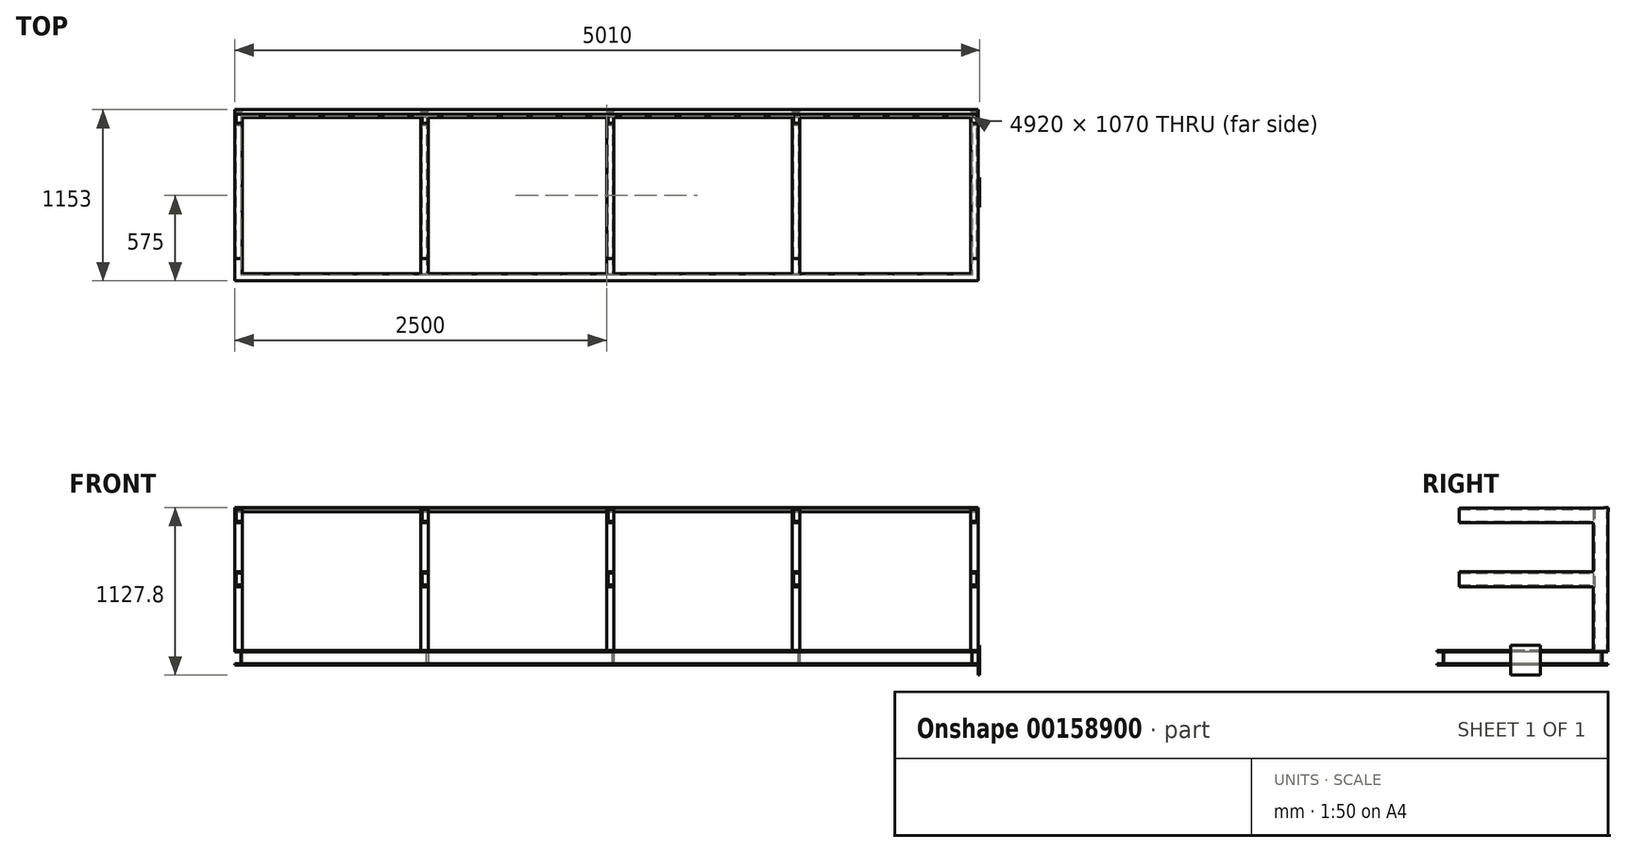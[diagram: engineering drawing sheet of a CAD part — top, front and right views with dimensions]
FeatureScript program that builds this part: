
annotation { "Feature Type Name" : "Feature", "Feature Type Description" : "" }
export const myFeature = defineFeature(function(context is Context, id is Id, definition is map)
    precondition{}
    {
        {
            var Q0;
            Q0=qCreatedBy(makeId("Top.planeOp"),FACE);
            var sketch = newSketch(context, id + "F0", { "sketchPlane" : qUnion([Q0])});
            skLineSegment(sketch, "E0.rect.bottom", {"start": v(2500, 550) * mm, "end": v(-2500, 550) * mm});
            skLineSegment(sketch, "E0.rect.top", {"start": v(2500, -600) * mm, "end": v(-2500, -600) * mm});
            skLineSegment(sketch, "E0.rect.left", {"start": v(2500, 550) * mm, "end": v(2500, -600) * mm});
            skLineSegment(sketch, "E0.rect.right", {"start": v(-2500, 550) * mm, "end": v(-2500, -600) * mm});
            skPoint(sketch, "E0.rect.middle", {"position": v(0, 0) * mm});
            skLineSegment(sketch, "E1.rect.left", {"start": v(2450, 500) * mm, "end": v(2450, -550) * mm});
            skLineSegment(sketch, "E1.rect.right", {"start": v(-2450, 500) * mm, "end": v(-2450, -550) * mm});
            skLineSegment(sketch, "E2.trimOffspring", {"start": v(2450, 500) * mm, "end": v(-2450, 500) * mm});
            skLineSegment(sketch, "E3.trimOffspring", {"start": v(2450, -550) * mm, "end": v(-2450, -550) * mm});
            skSolve(sketch);
        }
        {
            var Q0;
            Q0=makeQuery(id+"F0.imprint","IMPRINT",FACE,{"disambiguationData":[TD([[makeQuery(id+"F0.imprint","IMPRINT",EDGE,{"derivedFrom":sQuery(id+"F0.wireOp",EDGE,"E0.rect.bottom")}),1.0]])]});
            var Q1;
            {var subQ0=sQuery(id+"F0.wireOp",EDGE,"US4hY1gF-BCMl-q7YX-FSme-i0m9YlaeEOpe");Q1=makeQuery(id+"F0.imprint","IMPRINT",FACE,{"disambiguationData":[TD([[makeQuery(id+"F0.imprint","IMPRINT",EDGE,{"derivedFrom":subQ0}),1.0]])]});}
            extrude(context, id + "F1", {"entities" : qUnion([Q0, Q1]), "depth" : 100 * mm});
        }
        {
            var Q0;
            Q0=makeQuery(id+"F1.opExtrude","SWEPT_FACE",FACE,{"disambiguationData":[OSD([sQuery(id+"F0.wireOp",EDGE,"E0.rect.right")])]});
            var sketch = newSketch(context, id + "F2", { "sketchPlane" : qUnion([Q0])});
            skLineSegment(sketch, "E4.bottom", {"start": v(-550, 90) * mm, "end": v(-510, 90) * mm});
            skLineSegment(sketch, "E4.top", {"start": v(-550, 10) * mm, "end": v(-510, 10) * mm});
            skLineSegment(sketch, "E4.left", {"start": v(-550, 90) * mm, "end": v(-550, 10) * mm});
            skLineSegment(sketch, "E4.right", {"start": v(-510, 90) * mm, "end": v(-510, 10) * mm});
            skLineSegment(sketch, "E5.bottom", {"start": v(600, 90) * mm, "end": v(560, 90) * mm});
            skLineSegment(sketch, "E5.top", {"start": v(600, 10) * mm, "end": v(560, 10) * mm});
            skLineSegment(sketch, "E5.left", {"start": v(600, 90) * mm, "end": v(600, 10) * mm});
            skLineSegment(sketch, "E5.right", {"start": v(560, 90) * mm, "end": v(560, 10) * mm});
            skSolve(sketch);
        }
        {
            var Q0;
            Q0=makeQuery(id+"F2.imprint","IMPRINT",FACE,{"disambiguationData":[TD([[makeQuery(id+"F2.imprint","IMPRINT",EDGE,{"derivedFrom":sQuery(id+"F2.wireOp",EDGE,"E4.bottom")}),-1.0]])]});
            var Q1;
            Q1=makeQuery(id+"F2.imprint","IMPRINT",FACE,{"disambiguationData":[TD([[makeQuery(id+"F2.imprint","IMPRINT",EDGE,{"derivedFrom":sQuery(id+"F2.wireOp",EDGE,"E5.bottom")}),1.0]])]});
            extrude(context, id + "F3", {"entities" : qUnion([Q0, Q1]), "operationType" : NewBodyOperationType.REMOVE, "endBound" : BoundingType.THROUGH_ALL, "oppositeDirection" : true, "depth" : 25 * mm});
        }
        {
            var Q0;
            Q0=makeQuery(id+"F3.boolean.opBoolean","COPY",FACE,{"derivedFrom":makeQuery(id+"F3.opExtrude","SWEPT_FACE",FACE,{"disambiguationData":[OSD([sQuery(id+"F2.wireOp",EDGE,"E5.right")])]})});
            var sketch = newSketch(context, id + "F4", { "sketchPlane" : qUnion([Q0])});
            skLineSegment(sketch, "E6.bottom", {"start": v(2500, 90) * mm, "end": v(2460, 90) * mm});
            skLineSegment(sketch, "E6.top", {"start": v(2500, 10) * mm, "end": v(2460, 10) * mm});
            skLineSegment(sketch, "E6.left", {"start": v(2500, 90) * mm, "end": v(2500, 10) * mm});
            skLineSegment(sketch, "E6.right", {"start": v(2460, 90) * mm, "end": v(2460, 10) * mm});
            skLineSegment(sketch, "E7.bottom", {"start": v(-2500, 90) * mm, "end": v(-2460, 90) * mm});
            skLineSegment(sketch, "E7.top", {"start": v(-2500, 10) * mm, "end": v(-2460, 10) * mm});
            skLineSegment(sketch, "E7.left", {"start": v(-2500, 90) * mm, "end": v(-2500, 10) * mm});
            skLineSegment(sketch, "E7.right", {"start": v(-2460, 90) * mm, "end": v(-2460, 10) * mm});
            skSolve(sketch);
        }
        {
            var Q0;
            Q0=makeQuery(id+"F4.imprint","IMPRINT",FACE,{"disambiguationData":[TD([[makeQuery(id+"F4.imprint","IMPRINT",EDGE,{"derivedFrom":sQuery(id+"F4.wireOp",EDGE,"E6.bottom")}),1.0]])]});
            var Q1;
            Q1=makeQuery(id+"F4.imprint","IMPRINT",FACE,{"disambiguationData":[TD([[makeQuery(id+"F4.imprint","IMPRINT",EDGE,{"derivedFrom":sQuery(id+"F4.wireOp",EDGE,"E7.bottom")}),1.0]])]});
            extrude(context, id + "F5", {"entities" : qUnion([Q0, Q1]), "operationType" : NewBodyOperationType.REMOVE, "endBound" : BoundingType.THROUGH_ALL, "oppositeDirection" : true, "depth" : 25 * mm});
        }
        {
            var Q0;
            Q0=makeQuery(id+"F1.opExtrude","SWEPT_FACE",FACE,{"disambiguationData":[OSD([sQuery(id+"F0.wireOp",EDGE,"E2.trimOffspring")])]});
            var Q1;
            Q1=makeQuery(id+"F1.opExtrude","SWEPT_FACE",FACE,{"disambiguationData":[OSD([sQuery(id+"F0.wireOp",EDGE,"E2.trimOffspring")])]});
            var sketch = newSketch(context, id + "F6", { "sketchPlane" : qUnion([Q0, Q1])});
            skLineSegment(sketch, "E8.top", {"start": v(-1210, 90) * mm, "end": v(-1250, 90) * mm});
            skLineSegment(sketch, "E8.left", {"start": v(-1210, 9.97) * mm, "end": v(-1210, 90) * mm});
            skLineSegment(sketch, "E9", {"start": v(-1200, 100) * mm, "end": v(-1200, -0.03) * mm});
            skLineSegment(sketch, "E10", {"start": v(-1200, -0.03) * mm, "end": v(-1250, -0.03) * mm});
            skLineSegment(sketch, "E11", {"start": v(-1250, -0.03) * mm, "end": v(-1250, 9.97) * mm});
            skLineSegment(sketch, "E12", {"start": v(-1200, 100) * mm, "end": v(-1250, 100) * mm});
            skLineSegment(sketch, "E13", {"start": v(-1250, 100) * mm, "end": v(-1250, 90) * mm});
            skLineSegment(sketch, "E14.trimOffspring", {"start": v(-1210, 9.97) * mm, "end": v(-1250, 9.97) * mm});
            skLineSegment(sketch, "E15.1.0.0", {"start": v(40, 90) * mm, "end": v(0, 90) * mm});
            skLineSegment(sketch, "E15.1.0.1", {"start": v(40, 9.97) * mm, "end": v(0, 9.97) * mm});
            skLineSegment(sketch, "E15.1.0.2", {"start": v(50, 100) * mm, "end": v(50, -0.03) * mm});
            skLineSegment(sketch, "E15.1.0.3", {"start": v(50, -0.03) * mm, "end": v(0, -0.03) * mm});
            skLineSegment(sketch, "E15.1.0.4", {"start": v(40, 9.97) * mm, "end": v(40, 90) * mm});
            skLineSegment(sketch, "E15.1.0.5", {"start": v(50, 100) * mm, "end": v(0, 100) * mm});
            skLineSegment(sketch, "E15.1.0.6", {"start": v(0, 100) * mm, "end": v(0, 90) * mm});
            skLineSegment(sketch, "E15.1.0.7", {"start": v(0, -0.03) * mm, "end": v(0, 9.97) * mm});
            skLineSegment(sketch, "E15.2.0.0", {"start": v(1290, 90) * mm, "end": v(1250, 90) * mm});
            skLineSegment(sketch, "E15.2.0.1", {"start": v(1290, 9.97) * mm, "end": v(1250, 9.97) * mm});
            skLineSegment(sketch, "E15.2.0.2", {"start": v(1300, 100) * mm, "end": v(1300, -0.03) * mm});
            skLineSegment(sketch, "E15.2.0.3", {"start": v(1300, -0.03) * mm, "end": v(1250, -0.03) * mm});
            skLineSegment(sketch, "E15.2.0.4", {"start": v(1290, 9.97) * mm, "end": v(1290, 90) * mm});
            skLineSegment(sketch, "E15.2.0.5", {"start": v(1300, 100) * mm, "end": v(1250, 100) * mm});
            skLineSegment(sketch, "E15.2.0.6", {"start": v(1250, 100) * mm, "end": v(1250, 90) * mm});
            skLineSegment(sketch, "E15.2.0.7", {"start": v(1250, -0.03) * mm, "end": v(1250, 9.97) * mm});
            skLineSegment(sketch, "E15.direction1", {"start": v(-1250, -0.03) * mm, "end": v(0, -0.03) * mm, "construction": true});
            skSolve(sketch);
        }
        {
            var Q0;
            Q0=makeQuery(id+"F6.imprint","IMPRINT",FACE,{"disambiguationData":[TD([[makeQuery(id+"F6.imprint","IMPRINT",EDGE,{"derivedFrom":sQuery(id+"F6.wireOp",EDGE,"E8.top")}),-1.0]])]});
            var Q1;
            Q1=makeQuery(id+"F6.imprint","IMPRINT",FACE,{"disambiguationData":[TD([[makeQuery(id+"F6.imprint","IMPRINT",EDGE,{"derivedFrom":sQuery(id+"F6.wireOp",EDGE,"E15.1.0.0")}),-1.0]])]});
            var Q2;
            Q2=makeQuery(id+"F6.imprint","IMPRINT",FACE,{"disambiguationData":[TD([[makeQuery(id+"F6.imprint","IMPRINT",EDGE,{"derivedFrom":sQuery(id+"F6.wireOp",EDGE,"E15.2.0.0")}),-1.0]])]});
            var Q3;
            Q3=makeQuery(id+"F6.imprint","IMPRINT",FACE,{"disambiguationData":[TD([[makeQuery(id+"F6.imprint","IMPRINT",EDGE,{"derivedFrom":sQuery(id+"F6.wireOp",EDGE,"E8.top")}),-1.0]])]});
            var Q4;
            Q4=makeQuery(id+"F6.imprint","IMPRINT",FACE,{"disambiguationData":[TD([[makeQuery(id+"F6.imprint","IMPRINT",EDGE,{"derivedFrom":sQuery(id+"F6.wireOp",EDGE,"E15.1.0.0")}),-1.0]])]});
            var Q5;
            Q5=makeQuery(id+"F6.imprint","IMPRINT",FACE,{"disambiguationData":[TD([[makeQuery(id+"F6.imprint","IMPRINT",EDGE,{"derivedFrom":sQuery(id+"F6.wireOp",EDGE,"E15.2.0.0")}),-1.0]])]});
            var Q6;
            Q6=makeQuery(id+"F1.opExtrude","SWEPT_FACE",FACE,{"disambiguationData":[OSD([sQuery(id+"F0.wireOp",EDGE,"E3.trimOffspring")])]});
            extrude(context, id + "F7", {"entities" : qUnion([Q0, Q1, Q2, Q3, Q4, Q5]), "operationType" : NewBodyOperationType.ADD, "endBound" : BoundingType.UP_TO_NEXT, "oppositeDirection" : true, "depth" : 1150 * mm, "hasSecondDirection" : true, "secondDirectionBound" : SecondDirectionBoundingType.UP_TO_SURFACE, "secondDirectionOppositeDirection" : false, "secondDirectionBoundEntityFace" : qUnion([Q6]), "secondDirectionDepth" : 25 * mm});
        }
        {
            var Q0;
            Q0=makeQuery(id+"F1.opExtrude","CAP_FACE",FACE,{"disambiguationData":[OSD([sQuery(id+"F0.wireOp",EDGE,"E0.rect.bottom"),sQuery(id+"F0.wireOp",EDGE,"E0.rect.top"),sQuery(id+"F0.wireOp",EDGE,"E0.rect.left"),sQuery(id+"F0.wireOp",EDGE,"E0.rect.right"),sQuery(id+"F0.wireOp",EDGE,"E1.rect.bottom"),sQuery(id+"F0.wireOp",EDGE,"E1.rect.top"),sQuery(id+"F0.wireOp",EDGE,"E1.rect.left"),sQuery(id+"F0.wireOp",EDGE,"E1.rect.right"),sQuery(id+"F0.wireOp",EDGE,"169e65ff-8b3f-41cf-b013-59d8eb9306a3.rect.left"),sQuery(id+"F0.wireOp",EDGE,"169e65ff-8b3f-41cf-b013-59d8eb9306a3.rect.right"),sQuery(id+"F0.wireOp",EDGE,"E2.trimOffspring"),sQuery(id+"F0.wireOp",EDGE,"E3.trimOffspring"),sQuery(id+"F0.wireOp",EDGE,"US4hY1gF-BCMl-q7YX-FSme-i0m9YlaeEOpe"),sQuery(id+"F0.wireOp",EDGE,"PFxx0pdg-LAYr-f2aU-oRcx-HOFaLq6uxK7R")])],"isStart":false});
            var sketch = newSketch(context, id + "F8", { "sketchPlane" : qUnion([Q0])});
            skLineSegment(sketch, "E16.bottom", {"start": v(-2500, 550) * mm, "end": v(-2450, 550) * mm});
            skLineSegment(sketch, "E16.top", {"start": v(-2500, 450) * mm, "end": v(-2450, 450) * mm});
            skLineSegment(sketch, "E16.left", {"start": v(-2500, 550) * mm, "end": v(-2500, 450) * mm});
            skLineSegment(sketch, "E16.right", {"start": v(-2450, 550) * mm, "end": v(-2450, 540) * mm});
            skLineSegment(sketch, "E17.bottom", {"start": v(2500, 550) * mm, "end": v(2450, 550) * mm});
            skLineSegment(sketch, "E17.top", {"start": v(2500, 450) * mm, "end": v(2450, 450) * mm});
            skLineSegment(sketch, "E17.left", {"start": v(2500, 550) * mm, "end": v(2500, 450) * mm});
            skLineSegment(sketch, "E17.right", {"start": v(2450, 550) * mm, "end": v(2450, 540) * mm});
            skLineSegment(sketch, "E18", {"start": v(-2490, 540) * mm, "end": v(-2490, 460) * mm});
            skLineSegment(sketch, "E19", {"start": v(-2490, 460) * mm, "end": v(-2450, 460) * mm});
            skLineSegment(sketch, "E20", {"start": v(-2490, 540) * mm, "end": v(-2450, 540) * mm});
            skLineSegment(sketch, "E21.trimOffspring", {"start": v(-2450, 460) * mm, "end": v(-2450, 450) * mm});
            skLineSegment(sketch, "E22", {"start": v(2450, 540) * mm, "end": v(2490, 540) * mm});
            skLineSegment(sketch, "E23", {"start": v(2490, 540) * mm, "end": v(2490, 460) * mm});
            skLineSegment(sketch, "E24", {"start": v(2490, 460) * mm, "end": v(2450, 460) * mm});
            skLineSegment(sketch, "E25.trimOffspring", {"start": v(2450, 460) * mm, "end": v(2450, 450) * mm});
            skLineSegment(sketch, "E26.1.0.0", {"start": v(-1250, 550) * mm, "end": v(-1250, 450) * mm});
            skLineSegment(sketch, "E26.1.0.1", {"start": v(-1250, 450) * mm, "end": v(-1200, 450) * mm});
            skLineSegment(sketch, "E26.1.0.2", {"start": v(-1200, 460) * mm, "end": v(-1200, 450) * mm});
            skLineSegment(sketch, "E26.1.0.3", {"start": v(-1240, 460) * mm, "end": v(-1200, 460) * mm});
            skLineSegment(sketch, "E26.1.0.4", {"start": v(-1240, 540) * mm, "end": v(-1240, 460) * mm});
            skLineSegment(sketch, "E26.1.0.5", {"start": v(-1250, 550) * mm, "end": v(-1200, 550) * mm});
            skLineSegment(sketch, "E26.1.0.6", {"start": v(-1200, 550) * mm, "end": v(-1200, 540) * mm});
            skLineSegment(sketch, "E26.1.0.7", {"start": v(-1240, 540) * mm, "end": v(-1200, 540) * mm});
            skLineSegment(sketch, "E26.2.0.0", {"start": v(0, 550) * mm, "end": v(0, 450) * mm});
            skLineSegment(sketch, "E26.2.0.1", {"start": v(0, 450) * mm, "end": v(50, 450) * mm});
            skLineSegment(sketch, "E26.2.0.2", {"start": v(50, 460) * mm, "end": v(50, 450) * mm});
            skLineSegment(sketch, "E26.2.0.3", {"start": v(10, 460) * mm, "end": v(50, 460) * mm});
            skLineSegment(sketch, "E26.2.0.4", {"start": v(10, 540) * mm, "end": v(10, 460) * mm});
            skLineSegment(sketch, "E26.2.0.5", {"start": v(0, 550) * mm, "end": v(50, 550) * mm});
            skLineSegment(sketch, "E26.2.0.6", {"start": v(50, 550) * mm, "end": v(50, 540) * mm});
            skLineSegment(sketch, "E26.2.0.7", {"start": v(10, 540) * mm, "end": v(50, 540) * mm});
            skLineSegment(sketch, "E26.direction1", {"start": v(-2500, 450) * mm, "end": v(-1250, 450) * mm, "construction": true});
            skLineSegment(sketch, "E27.0.3.0", {"start": v(1250, 550) * mm, "end": v(1250, 450) * mm});
            skLineSegment(sketch, "E27.3.3.0", {"start": v(1250, 450) * mm, "end": v(1300, 450) * mm});
            skLineSegment(sketch, "E27.6.3.0", {"start": v(1300, 460) * mm, "end": v(1300, 450) * mm});
            skLineSegment(sketch, "E27.9.3.0", {"start": v(1260, 460) * mm, "end": v(1300, 460) * mm});
            skLineSegment(sketch, "E27.12.3.0", {"start": v(1260, 540) * mm, "end": v(1260, 460) * mm});
            skLineSegment(sketch, "E27.15.3.0", {"start": v(1250, 550) * mm, "end": v(1300, 550) * mm});
            skLineSegment(sketch, "E27.18.3.0", {"start": v(1300, 550) * mm, "end": v(1300, 540) * mm});
            skLineSegment(sketch, "E27.21.3.0", {"start": v(1260, 540) * mm, "end": v(1300, 540) * mm});
            skSolve(sketch);
        }
        {
            var Q0;
            {var subQ0=sQuery(id+"F8.wireOp",EDGE,"E26.1.0.5");Q0=makeQuery(id+"F8.imprint","IMPRINT",FACE,{"disambiguationData":[TD([[makeQuery(id+"F8.imprint","IMPRINT",EDGE,{"derivedFrom":subQ0}),1.0]])]});}
            var Q1;
            {var subQ1=sQuery(id+"F8.wireOp",EDGE,"E26.1.0.1");Q1=makeQuery(id+"F8.imprint","IMPRINT",FACE,{"disambiguationData":[TD([[makeQuery(id+"F8.imprint","IMPRINT",EDGE,{"derivedFrom":subQ1}),1.0]])]});}
            var Q2;
            Q2=makeQuery(id+"F8.imprint","IMPRINT",FACE,{"disambiguationData":[TD([[makeQuery(id+"F8.imprint","IMPRINT",EDGE,{"derivedFrom":sQuery(id+"F8.wireOp",EDGE,"E16.bottom")}),1.0]])]});
            var Q3;
            {var subQ1=sQuery(id+"F8.wireOp",EDGE,"E26.2.0.1");Q3=makeQuery(id+"F8.imprint","IMPRINT",FACE,{"disambiguationData":[TD([[makeQuery(id+"F8.imprint","IMPRINT",EDGE,{"derivedFrom":subQ1}),1.0]])]});}
            var Q4;
            {var subQ0=sQuery(id+"F8.wireOp",EDGE,"E26.2.0.5");Q4=makeQuery(id+"F8.imprint","IMPRINT",FACE,{"disambiguationData":[TD([[makeQuery(id+"F8.imprint","IMPRINT",EDGE,{"derivedFrom":subQ0}),1.0]])]});}
            var Q5;
            {var subQ0=sQuery(id+"F8.wireOp",EDGE,"E27.15.3.0");Q5=makeQuery(id+"F8.imprint","IMPRINT",FACE,{"disambiguationData":[TD([[makeQuery(id+"F8.imprint","IMPRINT",EDGE,{"derivedFrom":subQ0}),1.0]])]});}
            var Q6;
            {var subQ6=sQuery(id+"F8.wireOp",EDGE,"E27.3.3.0");Q6=makeQuery(id+"F8.imprint","IMPRINT",FACE,{"disambiguationData":[TD([[makeQuery(id+"F8.imprint","IMPRINT",EDGE,{"derivedFrom":subQ6}),1.0]])]});}
            var Q7;
            Q7=makeQuery(id+"F8.imprint","IMPRINT",FACE,{"disambiguationData":[TD([[makeQuery(id+"F8.imprint","IMPRINT",EDGE,{"derivedFrom":sQuery(id+"F8.wireOp",EDGE,"E17.bottom")}),1.0]])]});
            extrude(context, id + "F9", {"entities" : qUnion([Q0, Q1, Q2, Q3, Q4, Q5, Q6, Q7]), "operationType" : NewBodyOperationType.ADD, "depth" : 960 * mm});
        }
        {
            var Q0;
            Q0=makeQuery(id+"F9.opExtrude","SWEPT_FACE",FACE,{"disambiguationData":[OSD([sQuery(id+"F8.wireOp",EDGE,"E16.top")])]});
            cPlane(context, id + "F10", {"entities" : qUnion([Q0]), "cplaneType" : CPlaneType.OFFSET, "offset" : 0 * mm, "width" : 150 * mm, "height" : 150 * mm});
        }
        {
            var Q0;
            Q0=qCreatedBy(id+"F10.planeOp",FACE);
            var sketch = newSketch(context, id + "F11", { "sketchPlane" : qUnion([Q0])});
            skLineSegment(sketch, "E28.bottom", {"start": v(-2500, 630) * mm, "end": v(-2450, 630) * mm});
            skLineSegment(sketch, "E28.top", {"start": v(-2500, 530) * mm, "end": v(-2450, 530) * mm});
            skLineSegment(sketch, "E28.left", {"start": v(-2500, 630) * mm, "end": v(-2500, 530) * mm});
            skLineSegment(sketch, "E28.right", {"start": v(-2450, 630) * mm, "end": v(-2450, 620) * mm});
            skLineSegment(sketch, "E29.bottom", {"start": v(2450, 630) * mm, "end": v(2500, 630) * mm});
            skLineSegment(sketch, "E29.top", {"start": v(2450, 530) * mm, "end": v(2500, 530) * mm});
            skLineSegment(sketch, "E29.left", {"start": v(2450, 630) * mm, "end": v(2450, 620) * mm});
            skLineSegment(sketch, "E29.right", {"start": v(2500, 630) * mm, "end": v(2500, 530) * mm});
            skLineSegment(sketch, "E30", {"start": v(-2450, 620) * mm, "end": v(-2490, 620) * mm});
            skLineSegment(sketch, "E31", {"start": v(-2490, 620) * mm, "end": v(-2490, 540) * mm});
            skLineSegment(sketch, "E32", {"start": v(-2490, 540) * mm, "end": v(-2450, 540) * mm});
            skLineSegment(sketch, "E33.trimOffspring", {"start": v(-2450, 540) * mm, "end": v(-2450, 530) * mm});
            skLineSegment(sketch, "E34", {"start": v(2450, 620) * mm, "end": v(2490, 620) * mm});
            skLineSegment(sketch, "E35", {"start": v(2490, 620) * mm, "end": v(2490, 540) * mm});
            skLineSegment(sketch, "E36", {"start": v(2490, 540) * mm, "end": v(2450, 540) * mm});
            skLineSegment(sketch, "E37.trimOffspring", {"start": v(2450, 540) * mm, "end": v(2450, 530) * mm});
            skLineSegment(sketch, "E38.bottom", {"start": v(-2500, 1060) * mm, "end": v(-2450, 1060) * mm});
            skLineSegment(sketch, "E38.top", {"start": v(-2500, 960) * mm, "end": v(-2450, 960) * mm});
            skLineSegment(sketch, "E38.left", {"start": v(-2500, 1060) * mm, "end": v(-2500, 960) * mm});
            skLineSegment(sketch, "E38.right", {"start": v(-2450, 1060) * mm, "end": v(-2450, 1050) * mm});
            skLineSegment(sketch, "E39", {"start": v(-2450, 1050) * mm, "end": v(-2490, 1050) * mm});
            skLineSegment(sketch, "E40", {"start": v(-2490, 1050) * mm, "end": v(-2490, 970) * mm});
            skLineSegment(sketch, "E41", {"start": v(-2490, 970) * mm, "end": v(-2450, 970) * mm});
            skLineSegment(sketch, "E42.trimOffspring", {"start": v(-2450, 970) * mm, "end": v(-2450, 960) * mm});
            skLineSegment(sketch, "E43.bottom", {"start": v(2450, 1060) * mm, "end": v(2500, 1060) * mm});
            skLineSegment(sketch, "E43.top", {"start": v(2450, 960) * mm, "end": v(2500, 960) * mm});
            skLineSegment(sketch, "E43.left", {"start": v(2450, 1060) * mm, "end": v(2450, 1050) * mm});
            skLineSegment(sketch, "E43.right", {"start": v(2500, 1060) * mm, "end": v(2500, 960) * mm});
            skLineSegment(sketch, "E44", {"start": v(2450, 1050) * mm, "end": v(2490, 1050) * mm});
            skLineSegment(sketch, "E45", {"start": v(2490, 1050) * mm, "end": v(2490, 970) * mm});
            skLineSegment(sketch, "E46", {"start": v(2490, 970) * mm, "end": v(2450, 970) * mm});
            skLineSegment(sketch, "E47.trimOffspring", {"start": v(2450, 970) * mm, "end": v(2450, 960) * mm});
            skLineSegment(sketch, "E48.1.0.0", {"start": v(-1250, 630) * mm, "end": v(-1250, 530) * mm});
            skLineSegment(sketch, "E48.1.0.1", {"start": v(-1240, 970) * mm, "end": v(-1200, 970) * mm});
            skLineSegment(sketch, "E48.1.0.2", {"start": v(-1200, 1060) * mm, "end": v(-1200, 1050) * mm});
            skLineSegment(sketch, "E48.1.0.3", {"start": v(-1250, 960) * mm, "end": v(-1200, 960) * mm});
            skLineSegment(sketch, "E48.1.0.4", {"start": v(-1250, 1060) * mm, "end": v(-1200, 1060) * mm});
            skLineSegment(sketch, "E48.1.0.5", {"start": v(-1200, 1050) * mm, "end": v(-1240, 1050) * mm});
            skLineSegment(sketch, "E48.1.0.6", {"start": v(-1250, 1060) * mm, "end": v(-1250, 960) * mm});
            skLineSegment(sketch, "E48.1.0.7", {"start": v(-1240, 1050) * mm, "end": v(-1240, 970) * mm});
            skLineSegment(sketch, "E48.1.0.8", {"start": v(-1200, 970) * mm, "end": v(-1200, 960) * mm});
            skLineSegment(sketch, "E48.1.0.9", {"start": v(-1200, 540) * mm, "end": v(-1200, 530) * mm});
            skLineSegment(sketch, "E48.1.0.10", {"start": v(-1250, 530) * mm, "end": v(-1200, 530) * mm});
            skLineSegment(sketch, "E48.1.0.11", {"start": v(-1240, 540) * mm, "end": v(-1200, 540) * mm});
            skLineSegment(sketch, "E48.1.0.12", {"start": v(-1250, 630) * mm, "end": v(-1200, 630) * mm});
            skLineSegment(sketch, "E48.1.0.13", {"start": v(-1240, 620) * mm, "end": v(-1240, 540) * mm});
            skLineSegment(sketch, "E48.1.0.14", {"start": v(-1200, 620) * mm, "end": v(-1240, 620) * mm});
            skLineSegment(sketch, "E48.1.0.15", {"start": v(-1200, 630) * mm, "end": v(-1200, 620) * mm});
            skLineSegment(sketch, "E48.2.0.0", {"start": v(0, 630) * mm, "end": v(0, 530) * mm});
            skLineSegment(sketch, "E48.2.0.1", {"start": v(10, 970) * mm, "end": v(50, 970) * mm});
            skLineSegment(sketch, "E48.2.0.2", {"start": v(50, 1060) * mm, "end": v(50, 1050) * mm});
            skLineSegment(sketch, "E48.2.0.3", {"start": v(0, 960) * mm, "end": v(50, 960) * mm});
            skLineSegment(sketch, "E48.2.0.4", {"start": v(0, 1060) * mm, "end": v(50, 1060) * mm});
            skLineSegment(sketch, "E48.2.0.5", {"start": v(50, 1050) * mm, "end": v(10, 1050) * mm});
            skLineSegment(sketch, "E48.2.0.6", {"start": v(0, 1060) * mm, "end": v(0, 960) * mm});
            skLineSegment(sketch, "E48.2.0.7", {"start": v(10, 1050) * mm, "end": v(10, 970) * mm});
            skLineSegment(sketch, "E48.2.0.8", {"start": v(50, 970) * mm, "end": v(50, 960) * mm});
            skLineSegment(sketch, "E48.2.0.9", {"start": v(50, 540) * mm, "end": v(50, 530) * mm});
            skLineSegment(sketch, "E48.2.0.10", {"start": v(0, 530) * mm, "end": v(50, 530) * mm});
            skLineSegment(sketch, "E48.2.0.11", {"start": v(10, 540) * mm, "end": v(50, 540) * mm});
            skLineSegment(sketch, "E48.2.0.12", {"start": v(0, 630) * mm, "end": v(50, 630) * mm});
            skLineSegment(sketch, "E48.2.0.13", {"start": v(10, 620) * mm, "end": v(10, 540) * mm});
            skLineSegment(sketch, "E48.2.0.14", {"start": v(50, 620) * mm, "end": v(10, 620) * mm});
            skLineSegment(sketch, "E48.2.0.15", {"start": v(50, 630) * mm, "end": v(50, 620) * mm});
            skLineSegment(sketch, "E48.direction1", {"start": v(-2500, 530) * mm, "end": v(-1250, 530) * mm, "construction": true});
            skLineSegment(sketch, "E49.0.3.0", {"start": v(1250, 630) * mm, "end": v(1250, 530) * mm});
            skLineSegment(sketch, "E49.3.3.0", {"start": v(1260, 970) * mm, "end": v(1300, 970) * mm});
            skLineSegment(sketch, "E49.6.3.0", {"start": v(1300, 1060) * mm, "end": v(1300, 1050) * mm});
            skLineSegment(sketch, "E49.9.3.0", {"start": v(1250, 960) * mm, "end": v(1300, 960) * mm});
            skLineSegment(sketch, "E49.12.3.0", {"start": v(1250, 1060) * mm, "end": v(1300, 1060) * mm});
            skLineSegment(sketch, "E49.15.3.0", {"start": v(1300, 1050) * mm, "end": v(1260, 1050) * mm});
            skLineSegment(sketch, "E49.18.3.0", {"start": v(1250, 1060) * mm, "end": v(1250, 960) * mm});
            skLineSegment(sketch, "E49.21.3.0", {"start": v(1260, 1050) * mm, "end": v(1260, 970) * mm});
            skLineSegment(sketch, "E49.24.3.0", {"start": v(1300, 970) * mm, "end": v(1300, 960) * mm});
            skLineSegment(sketch, "E49.27.3.0", {"start": v(1300, 540) * mm, "end": v(1300, 530) * mm});
            skLineSegment(sketch, "E49.30.3.0", {"start": v(1250, 530) * mm, "end": v(1300, 530) * mm});
            skLineSegment(sketch, "E49.33.3.0", {"start": v(1260, 540) * mm, "end": v(1300, 540) * mm});
            skLineSegment(sketch, "E49.36.3.0", {"start": v(1250, 630) * mm, "end": v(1300, 630) * mm});
            skLineSegment(sketch, "E49.39.3.0", {"start": v(1260, 620) * mm, "end": v(1260, 540) * mm});
            skLineSegment(sketch, "E49.42.3.0", {"start": v(1300, 620) * mm, "end": v(1260, 620) * mm});
            skLineSegment(sketch, "E49.45.3.0", {"start": v(1300, 630) * mm, "end": v(1300, 620) * mm});
            skSolve(sketch);
        }
        {
            var Q0;
            Q0=makeQuery(id+"F11.imprint","IMPRINT",FACE,{"disambiguationData":[TD([[makeQuery(id+"F11.imprint","IMPRINT",EDGE,{"derivedFrom":sQuery(id+"F11.wireOp",EDGE,"E28.bottom")}),-1.0]])]});
            var Q1;
            Q1=makeQuery(id+"F11.imprint","IMPRINT",FACE,{"disambiguationData":[TD([[makeQuery(id+"F11.imprint","IMPRINT",EDGE,{"derivedFrom":sQuery(id+"F11.wireOp",EDGE,"XEhtTrfZ-fChM-jcK2-Cb9I-VW7ByfVid4v8.bottom")}),-1.0]])]});
            var Q2;
            Q2=makeQuery(id+"F11.imprint","IMPRINT",FACE,{"disambiguationData":[TD([[makeQuery(id+"F11.imprint","IMPRINT",EDGE,{"derivedFrom":sQuery(id+"F11.wireOp",EDGE,"R9ZixYyl-yBbL-hBKU-XpMU-qku1DJPLaCG0.bottom")}),-1.0]])]});
            var Q3;
            Q3=makeQuery(id+"F11.imprint","IMPRINT",FACE,{"disambiguationData":[TD([[makeQuery(id+"F11.imprint","IMPRINT",EDGE,{"derivedFrom":sQuery(id+"F11.wireOp",EDGE,"E29.bottom")}),-1.0]])]});
            var Q4;
            Q4=makeQuery(id+"F11.imprint","IMPRINT",FACE,{"disambiguationData":[TD([[makeQuery(id+"F11.imprint","IMPRINT",EDGE,{"derivedFrom":sQuery(id+"F11.wireOp",EDGE,"E48.1.0.0")}),1.0]])]});
            var Q5;
            Q5=makeQuery(id+"F11.imprint","IMPRINT",FACE,{"disambiguationData":[TD([[makeQuery(id+"F11.imprint","IMPRINT",EDGE,{"derivedFrom":sQuery(id+"F11.wireOp",EDGE,"E48.2.0.0")}),1.0]])]});
            var Q6;
            Q6=makeQuery(id+"F11.imprint","IMPRINT",FACE,{"disambiguationData":[TD([[makeQuery(id+"F11.imprint","IMPRINT",EDGE,{"derivedFrom":sQuery(id+"F11.wireOp",EDGE,"E49.0.3.0")}),1.0]])]});
            extrude(context, id + "F12", {"entities" : qUnion([Q0, Q1, Q2, Q3, Q4, Q5, Q6]), "operationType" : NewBodyOperationType.ADD, "depth" : 900 * mm});
        }
        {
            var Q0;
            Q0=makeQuery(id+"F11.imprint","IMPRINT",FACE,{"disambiguationData":[TD([[makeQuery(id+"F11.imprint","IMPRINT",EDGE,{"derivedFrom":sQuery(id+"F11.wireOp",EDGE,"E38.bottom")}),-1.0]])]});
            var Q1;
            Q1=makeQuery(id+"F11.imprint","IMPRINT",FACE,{"disambiguationData":[TD([[makeQuery(id+"F11.imprint","IMPRINT",EDGE,{"derivedFrom":sQuery(id+"F11.wireOp",EDGE,"ecd93ba5-6f4e-42af-942e-34594ae192be.bottom")}),-1.0]])]});
            var Q2;
            Q2=makeQuery(id+"F11.imprint","IMPRINT",FACE,{"disambiguationData":[TD([[makeQuery(id+"F11.imprint","IMPRINT",EDGE,{"derivedFrom":sQuery(id+"F11.wireOp",EDGE,"11143c5f-67a5-4754-a29c-3a1705a4cba4.bottom")}),-1.0]])]});
            var Q3;
            Q3=makeQuery(id+"F11.imprint","IMPRINT",FACE,{"disambiguationData":[TD([[makeQuery(id+"F11.imprint","IMPRINT",EDGE,{"derivedFrom":sQuery(id+"F11.wireOp",EDGE,"E43.bottom")}),-1.0]])]});
            var Q4;
            Q4=makeQuery(id+"F11.imprint","IMPRINT",FACE,{"disambiguationData":[TD([[makeQuery(id+"F11.imprint","IMPRINT",EDGE,{"derivedFrom":sQuery(id+"F11.wireOp",EDGE,"E48.1.0.1")}),-1.0]])]});
            var Q5;
            Q5=makeQuery(id+"F11.imprint","IMPRINT",FACE,{"disambiguationData":[TD([[makeQuery(id+"F11.imprint","IMPRINT",EDGE,{"derivedFrom":sQuery(id+"F11.wireOp",EDGE,"E48.2.0.1")}),-1.0]])]});
            var Q6;
            Q6=makeQuery(id+"F11.imprint","IMPRINT",FACE,{"disambiguationData":[TD([[makeQuery(id+"F11.imprint","IMPRINT",EDGE,{"derivedFrom":sQuery(id+"F11.wireOp",EDGE,"E49.3.3.0")}),-1.0]])]});
            extrude(context, id + "F13", {"entities" : qUnion([Q0, Q1, Q2, Q3, Q4, Q5, Q6]), "operationType" : NewBodyOperationType.ADD, "depth" : 900 * mm});
        }
        {
            var Q0;
            {var subQ1=sQuery(id+"F0.wireOp",EDGE,"E0.rect.left");Q0=makeQuery(id+"F13.boolean.opBoolean","MERGE",FACE,{"derivedFrom":[makeQuery(id+"F12.boolean.opBoolean","MERGE",FACE,{"derivedFrom":[makeQuery(id+"F9.boolean.opBoolean","MERGE",FACE,{"derivedFrom":[makeQuery(id+"F5.boolean.opBoolean","SPLIT",FACE,{"disambiguationData":[TD([makeQuery(id+"F3.boolean.opBoolean","COPY",FACE,{"derivedFrom":makeQuery(id+"F3.opExtrude","SWEPT_FACE",FACE,{"disambiguationData":[OSD([sQuery(id+"F2.wireOp",EDGE,"E4.bottom")])]})})])],"derivedFrom":makeQuery(id+"F1.opExtrude","SWEPT_FACE",FACE,{"disambiguationData":[OSD([subQ1])]})}),makeQuery(id+"F9.opExtrude","SWEPT_FACE",FACE,{"disambiguationData":[OSD([sQuery(id+"F8.wireOp",EDGE,"E17.left")])]})]}),makeQuery(id+"F12.opExtrude","SWEPT_FACE",FACE,{"disambiguationData":[OSD([sQuery(id+"F11.wireOp",EDGE,"E29.right")])]})]}),makeQuery(id+"F13.opExtrude","SWEPT_FACE",FACE,{"disambiguationData":[OSD([sQuery(id+"F11.wireOp",EDGE,"E43.right")])]})]});}
            var sketch = newSketch(context, id + "F14", { "sketchPlane" : qUnion([Q0])});
            skLineSegment(sketch, "E50.bottom", {"start": v(523, 1063) * mm, "end": v(553, 1063) * mm});
            skLineSegment(sketch, "E50.top", {"start": v(550, 1033) * mm, "end": v(553, 1033) * mm});
            skLineSegment(sketch, "E50.left", {"start": v(523, 1063) * mm, "end": v(523, 1060) * mm});
            skLineSegment(sketch, "E50.right", {"start": v(553, 1063) * mm, "end": v(553, 1033) * mm});
            skLineSegment(sketch, "E51", {"start": v(523, 1060) * mm, "end": v(550, 1060) * mm});
            skLineSegment(sketch, "E52", {"start": v(550, 1060) * mm, "end": v(550, 1033) * mm});
            skSolve(sketch);
        }
        {
            var Q0;
            Q0=makeQuery(id+"F14.imprint","IMPRINT",FACE,{"disambiguationData":[TD([[makeQuery(id+"F14.imprint","IMPRINT",EDGE,{"derivedFrom":sQuery(id+"F14.wireOp",EDGE,"E50.bottom")}),-1.0]])]});
            var Q1;
            Q1=makeQuery(id+"F9.opExtrude","SWEPT_FACE",FACE,{"disambiguationData":[OSD([sQuery(id+"F8.wireOp",EDGE,"E18")])]});
            extrude(context, id + "F15", {"entities" : qUnion([Q0]), "operationType" : NewBodyOperationType.ADD, "oppositeDirection" : true, "endBoundEntityFace" : qUnion([Q1]), "depth" : 5000 * mm});
        }
        {
            var Q0;
            {var subQ1=sQuery(id+"F0.wireOp",EDGE,"E0.rect.left");Q0=makeQuery(id+"F15.boolean.opBoolean","MERGE",FACE,{"derivedFrom":[makeQuery(id+"F13.boolean.opBoolean","MERGE",FACE,{"derivedFrom":[makeQuery(id+"F12.boolean.opBoolean","MERGE",FACE,{"derivedFrom":[makeQuery(id+"F9.boolean.opBoolean","MERGE",FACE,{"derivedFrom":[makeQuery(id+"F5.boolean.opBoolean","SPLIT",FACE,{"disambiguationData":[TD([makeQuery(id+"F3.boolean.opBoolean","COPY",FACE,{"derivedFrom":makeQuery(id+"F3.opExtrude","SWEPT_FACE",FACE,{"disambiguationData":[OSD([sQuery(id+"F2.wireOp",EDGE,"E4.bottom")])]})})])],"derivedFrom":makeQuery(id+"F1.opExtrude","SWEPT_FACE",FACE,{"disambiguationData":[OSD([subQ1])]})}),makeQuery(id+"F9.opExtrude","SWEPT_FACE",FACE,{"disambiguationData":[OSD([sQuery(id+"F8.wireOp",EDGE,"E17.left")])]})]}),makeQuery(id+"F12.opExtrude","SWEPT_FACE",FACE,{"disambiguationData":[OSD([sQuery(id+"F11.wireOp",EDGE,"E29.right")])]})]}),makeQuery(id+"F13.opExtrude","SWEPT_FACE",FACE,{"disambiguationData":[OSD([sQuery(id+"F11.wireOp",EDGE,"E43.right")])]})]}),makeQuery(id+"F15.opExtrude","CAP_FACE",FACE,{"disambiguationData":[OSD([sQuery(id+"F14.wireOp",EDGE,"E50.bottom"),sQuery(id+"F14.wireOp",EDGE,"E50.top"),sQuery(id+"F14.wireOp",EDGE,"E50.left"),sQuery(id+"F14.wireOp",EDGE,"E50.right"),sQuery(id+"F14.wireOp",EDGE,"E51"),sQuery(id+"F14.wireOp",EDGE,"E52")])],"isStart":true})]});}
            var sketch = newSketch(context, id + "F16", { "sketchPlane" : qUnion([Q0])});
            skLineSegment(sketch, "E53.bottom", {"start": v(-103.28, 135.2) * mm, "end": v(96.72, 135.2) * mm});
            skLineSegment(sketch, "E53.top", {"start": v(-103.28, -64.8) * mm, "end": v(96.72, -64.8) * mm});
            skLineSegment(sketch, "E53.left", {"start": v(-103.28, 135.2) * mm, "end": v(-103.28, -64.8) * mm});
            skLineSegment(sketch, "E53.right", {"start": v(96.72, 135.2) * mm, "end": v(96.72, -64.8) * mm});
            skSolve(sketch);
        }
        {
            var Q0;
            {var subQ0=sQuery(id+"F16.wireOp",EDGE,"E53.top");Q0=makeQuery(id+"F16.imprint","IMPRINT",FACE,{"disambiguationData":[TD([[makeQuery(id+"F16.imprint","IMPRINT",EDGE,{"derivedFrom":subQ0}),1.0]])]});}
            var Q1;
            {var subQ0=sQuery(id+"F16.wireOp",EDGE,"E53.bottom");Q1=makeQuery(id+"F16.imprint","IMPRINT",FACE,{"disambiguationData":[TD([[makeQuery(id+"F16.imprint","IMPRINT",EDGE,{"derivedFrom":subQ0}),-1.0]])]});}
            var Q2;
            {var subQ0=sQuery(id+"F16.wireOp",EDGE,"E53.left");var subQ1=sQuery(id+"F0.wireOp",EDGE,"E0.rect.left");var subQ2=makeQuery(id+"F1.opExtrude","CAP_EDGE",EDGE,{"disambiguationData":[OSD([subQ1])],"isStart":false});var subQ3=makeQuery(id+"F16.imprint","INTERSECT",VERTEX,{"derivedFrom":[subQ2,subQ0]});Q2=makeQuery(id+"F16.imprint","IMPRINT",FACE,{"disambiguationData":[TD([[makeQuery(id+"F16.imprint","IMPRINT",EDGE,{"disambiguationData":[TD([[subQ3,1.0]])],"derivedFrom":subQ2}),1.0]])]});}
            extrude(context, id + "F17", {"entities" : qUnion([Q0, Q1, Q2]), "operationType" : NewBodyOperationType.ADD, "depth" : 10 * mm});
        }
    });
